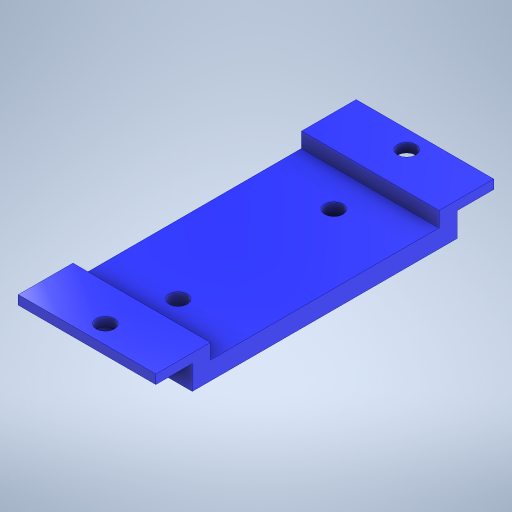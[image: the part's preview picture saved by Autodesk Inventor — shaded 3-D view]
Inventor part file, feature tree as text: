
AUTODESK INVENTOR PART (.ipt)
format: ipt  version: 2023 (Build 270158000, 158)  size: 371,200 bytes
history: native  units: mm
features: extrude x7, sketch x7
ambient origin geometry x8: Origin, YZ Plane, XZ Plane, XY Plane, X Axis, Y Axis, Z Axis, Center Point
bodies: Solid1 (feature_tree)
feature tree (14):
  extrude  "Extrusion1"  Depth=20.0mm
  extrude  "Extrusion2"  Depth=26.0mm
  extrude  "Extrusion3"  Depth=20.0mm
  extrude  "Extrusion4"  Depth=10.0mm
  sketch  "Sketch5"  dims[d9=10.0mm d10=26.0mm]
  extrude  "Extrusion5"  Depth=10.0mm
  extrude  "Extrusion6"  Depth=75.5mm TaperAngle=0.0deg
  extrude  "Extrusion7"  Depth=20.0mm
  sketch  "Sketch1"  dims[d0=20.0mm d1=20.0mm]
  sketch  "Sketch2"  dims[d2=55.5mm d3=26.0mm]
  sketch  "Sketch3"  dims[d5=20.0mm d6=45.5mm]
  sketch  "Sketch4"  dims[d7=20.0mm d8=10.0mm]
  sketch  "Sketch6"  dims[d11=75.5mm d12=0.0mm d13=75.5mm d14=0.0mm]
  sketch  "Sketch7"  dims[d21=65.5mm d22=55.5mm d23=10.0mm d24=10.0mm d25=0.0mm d26=0.0mm d27=18.25mm d28=0.0mm d29=0.0mm d30=5.0mm d31=5.0mm d32=20.0mm d33=0.0mm d34=20.0mm d35=0.0mm d36=10.0mm d37=10.0mm d38=20.0mm d39=0.0mm]
